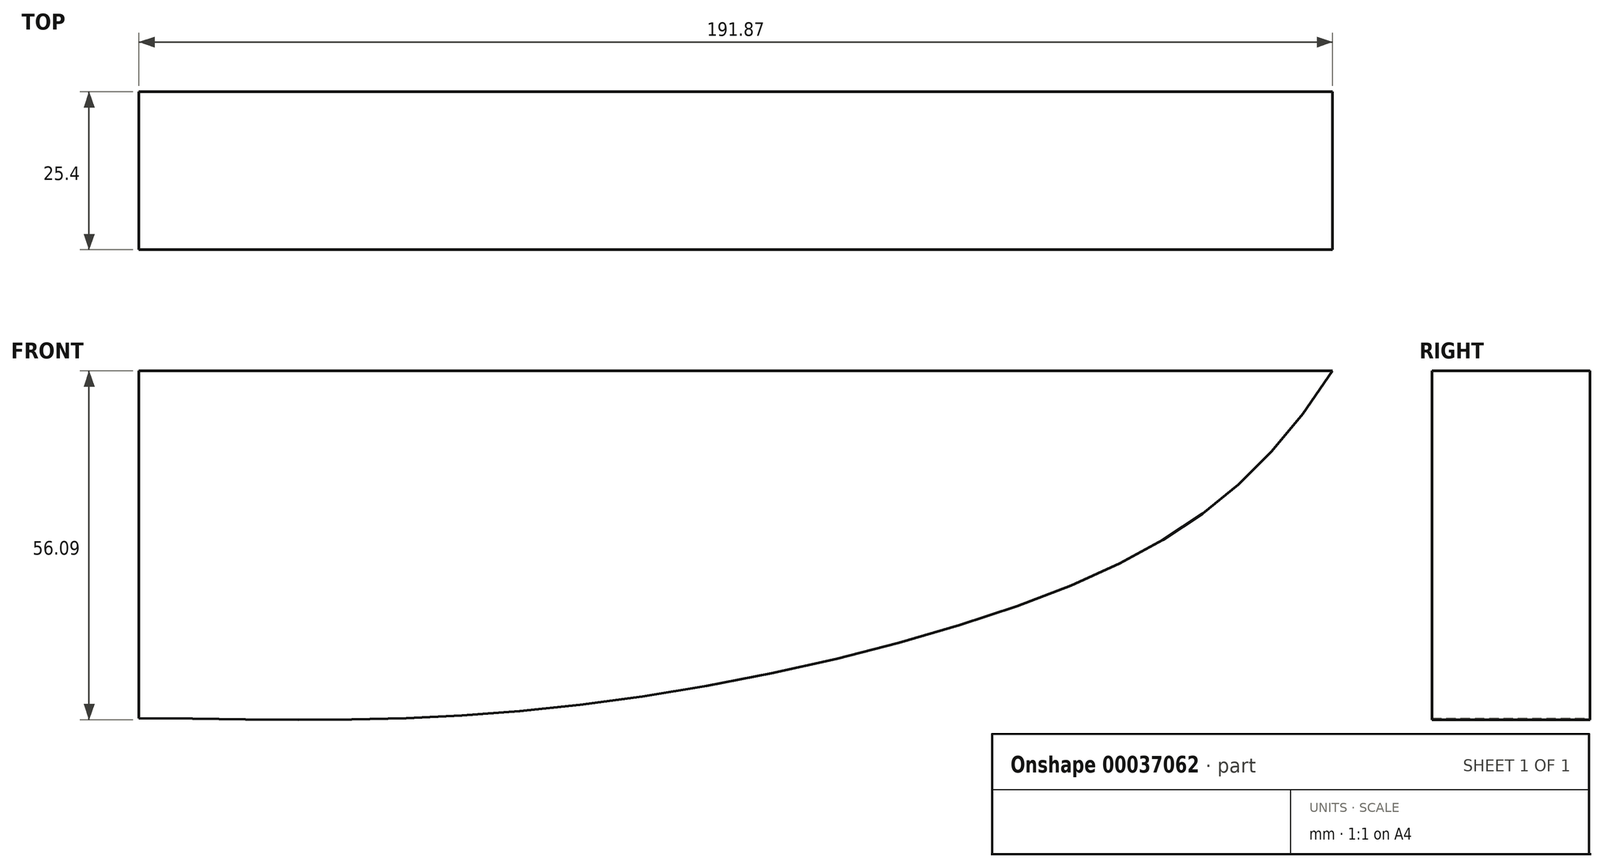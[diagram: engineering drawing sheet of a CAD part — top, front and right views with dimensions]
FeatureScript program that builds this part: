
annotation { "Feature Type Name" : "Feature", "Feature Type Description" : "" }
export const myFeature = defineFeature(function(context is Context, id is Id, definition is map)
    precondition{}
    {
        {
            var Q0;
            Q0=qCreatedBy(makeId("Front.planeOp"),FACE);
            var sketch = newSketch(context, id + "F0", { "sketchPlane" : qUnion([Q0])});
            skFitSpline(sketch, "E0", {"points": [v(62.2, 20.69) * mm, v(22.72, -12.7) * mm, v(-62.62, -33.45) * mm, v(-129.67, -35.15) * mm], "startDerivative": vector(-107.76, -168.83) * mm, "endDerivative": vector(-199.99, 1.64) * mm});
            skLineSegment(sketch, "E1", {"start": v(62.2, 20.69) * mm, "end": v(-129.67, 20.69) * mm});
            skLineSegment(sketch, "E2", {"start": v(-129.67, 20.69) * mm, "end": v(-129.67, -35.15) * mm});
            skSolve(sketch);
        }
        {
            var Q0;
            Q0 = qSketchRegion(id + "F0", true);
            extrude(context, id + "F1", {"entities" : qUnion([Q0]), "endBound" : BoundingType.SYMMETRIC, "depth" : 25.4 * mm});
        }
    });
